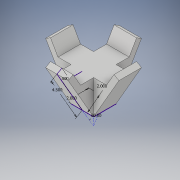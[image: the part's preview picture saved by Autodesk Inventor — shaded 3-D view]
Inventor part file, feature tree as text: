
AUTODESK INVENTOR PART (.ipt)
format: ipt  version: 2019 (Build 230136000, 136)  size: 128,000 bytes
history: native  units: in
note: dims shown in document units (in); Inventor stores cm internally (conversion verified against a paired STEP export)
features: extrude x2, sketch x2, pattern_circular x1
ambient origin geometry x8: Origin, YZ Plane, XZ Plane, XY Plane, X Axis, Y Axis, Z Axis, Center Point
bodies: Solid1 (feature_tree)
feature tree (5):
  extrude  "Extrusion1"  Depth=2.0in
  extrude  "Extrusion2"  Depth=2.0in TaperAngle=0.0deg
  pattern_circular  "Circular Pattern1"  Count=4 Angle=360.0deg
  sketch  "Sketch1"  dims[d0=2.0in d1=2.0in]
  sketch  "Sketch3"  dims[d2=3.0in d3=0.0in d8=2.0in d9=0.0in d10=1.5748in d11=360.0deg d14=60.0deg d15=0.5in d16=4.5in]
